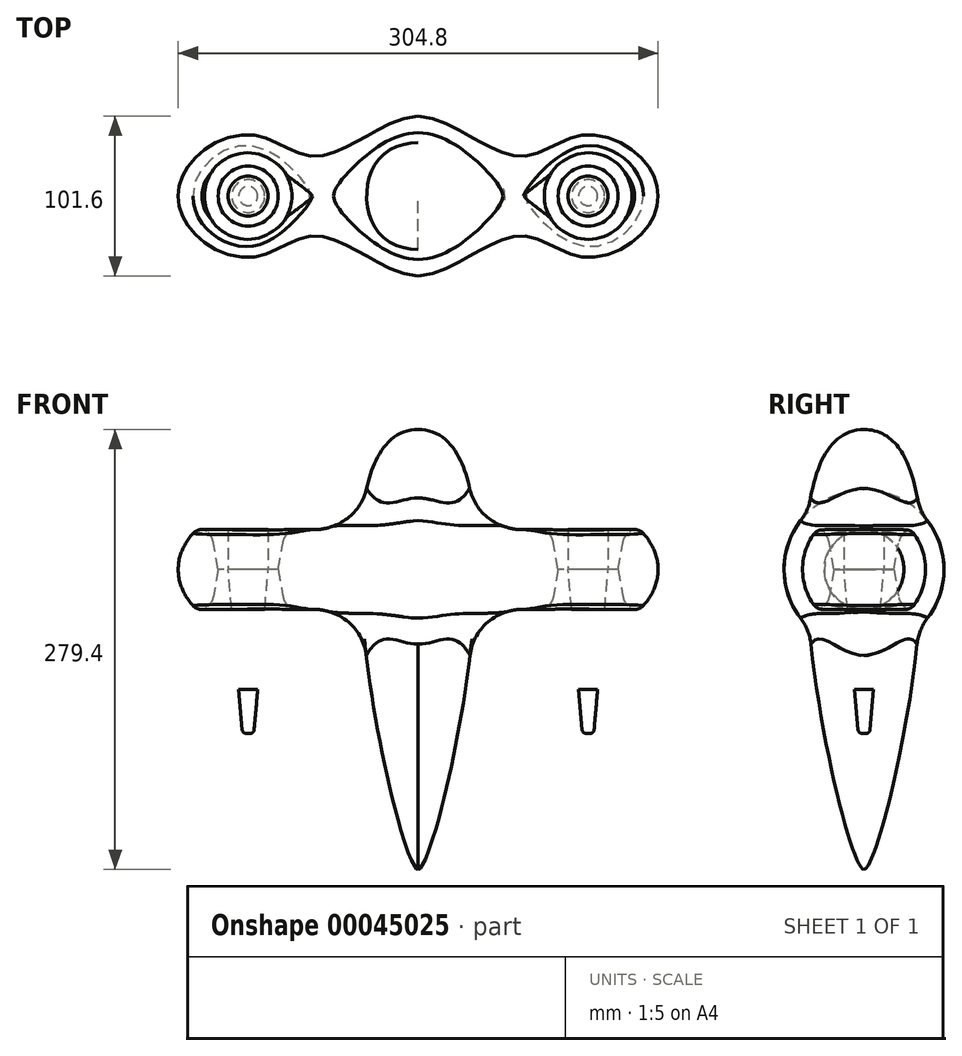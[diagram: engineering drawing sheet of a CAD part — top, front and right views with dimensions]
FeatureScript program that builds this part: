
annotation { "Feature Type Name" : "Feature", "Feature Type Description" : "" }
export const myFeature = defineFeature(function(context is Context, id is Id, definition is map)
    precondition{}
    {
        {
            var Q0;
            Q0=qCreatedBy(makeId("Front.planeOp"),FACE);
            var sketch = newSketch(context, id + "F0", { "sketchPlane" : qUnion([Q0])});
            skLineSegment(sketch, "E0", {"start": v(0, 0) * mm, "end": v(0, 0) * mm});
            skLineSegment(sketch, "E1", {"start": v(0, 0) * mm, "end": v(0, 50.8) * mm});
            skFitSpline(sketch, "E2", {"points": [v(0, 50.8) * mm, v(63.5, 25.4) * mm, v(107.95, 39) * mm, v(152.4, 0) * mm], "startDerivative": vector(157.4, 0) * mm, "endDerivative": vector(0, -203.14) * mm});
            skLineSegment(sketch, "E3", {"start": v(0, 0) * mm, "end": v(152.4, 0) * mm});
            skSolve(sketch);
        }
        {
            var Q0;
            Q0 = qSketchRegion(id + "F0", true);
            var Q1;
            Q1=sQuery(id+"F0.wireOp",EDGE,"E3");
            revolve(context, id + "F1", {"entities" : qUnion([Q0]), "axis" : qUnion([Q1]), "revolveType" : RevolveType.FULL});
        }
        {
            var Q0;
            Q0=makeQuery(id+"F1.opRevolve","SWEPT_BODY",BODY,{"disambiguationData":[OSD([sQuery(id+"F0.wireOp",EDGE,"E0"),sQuery(id+"F0.wireOp",EDGE,"E1"),sQuery(id+"F0.wireOp",EDGE,"E2"),sQuery(id+"F0.wireOp",EDGE,"E3")])]});
            var Q1;
            Q1=makeQuery(id+"F1.opRevolve","SWEPT_FACE",FACE,{"disambiguationData":[OSD([sQuery(id+"F0.wireOp",EDGE,"E1")])]});
            mirror(context, id + "F2", {"operationType" : NewBodyOperationType.ADD, "entities" : qUnion([Q0]), "mirrorPlane" : qUnion([Q1])});
        }
        {
            var Q0;
            Q0=qCreatedBy(makeId("Top.planeOp"),FACE);
            var sketch = newSketch(context, id + "F3", { "sketchPlane" : qUnion([Q0])});
            skCircle(sketch, "E4", {"center": v(-107.95, 0) * mm, "radius": 19.05 * mm});
            skCircle(sketch, "E5", {"center": v(107.95, 0) * mm, "radius": 19.05 * mm});
            skLineSegment(sketch, "E6", {"start": v(-107.95, 0) * mm, "end": v(107.95, 0) * mm, "construction": true});
            skSolve(sketch);
        }
        {
            var Q0;
            Q0 = qSketchRegion(id + "F3", true);
            extrude(context, id + "F4", {"entities" : qUnion([Q0]), "operationType" : NewBodyOperationType.REMOVE, "endBound" : BoundingType.THROUGH_ALL, "depth" : 76.2 * mm, "hasDraft" : true, "draftAngle" : 10 * degree, "hasSecondDirection" : true, "secondDirectionBound" : SecondDirectionBoundingType.THROUGH_ALL, "secondDirectionOppositeDirection" : true, "secondDirectionDepth" : 25.4 * mm, "hasSecondDirectionDraft" : true, "secondDirectionDraftAngle" : 10 * degree});
        }
        {
            var Q0;
            Q0=qCreatedBy(makeId("Top.planeOp"),FACE);
            var sketch = newSketch(context, id + "F5", { "sketchPlane" : qUnion([Q0])});
            skCircle(sketch, "E7", {"center": v(-107.95, 0) * mm, "radius": 12.7 * mm});
            skCircle(sketch, "E8", {"center": v(107.95, 0) * mm, "radius": 12.7 * mm});
            skSolve(sketch);
        }
        {
            var Q0;
            Q0 = qSketchRegion(id + "F5", true);
            extrude(context, id + "F6", {"entities" : qUnion([Q0]), "depth" : 50.8 * mm, "hasSecondDirection" : true, "secondDirectionOppositeDirection" : true, "secondDirectionDepth" : 104.14 * mm, "hasSecondDirectionDraft" : true, "secondDirectionDraftAngle" : 5 * degree, "secondDirectionDraftPullDirection" : true});
        }
        {
            var Q0;
            Q0=makeQuery(id+"F6.opExtrude","CAP_EDGE",EDGE,{"disambiguationData":[OSD([sQuery(id+"F5.wireOp",EDGE,"E7")])],"isStart":false});
            var Q1;
            Q1=makeQuery(id+"F6.opExtrude","CAP_EDGE",EDGE,{"disambiguationData":[OSD([sQuery(id+"F5.wireOp",EDGE,"E8")])],"isStart":false});
            fillet(context, id + "F7", {"entities" : qUnion([Q0, Q1]), "radius" : 12.7 * mm, "tangentPropagation" : true, "allowEdgeOverflow" : false});
        }
        {
            var Q0;
            Q0=makeQuery(id+"F6.opExtrude","CAP_EDGE",EDGE,{"disambiguationData":[OSD([sQuery(id+"F5.wireOp",EDGE,"E7")])],"isStart":true});
            var Q1;
            Q1=makeQuery(id+"F6.opExtrude","CAP_EDGE",EDGE,{"disambiguationData":[OSD([sQuery(id+"F5.wireOp",EDGE,"E8")])],"isStart":true});
            fillet(context, id + "F8", {"entities" : qUnion([Q0, Q1]), "radius" : 2.54 * mm, "tangentPropagation" : true, "allowEdgeOverflow" : false});
        }
        {
            var Q0;
            Q0=qCreatedBy(makeId("Right.planeOp"),FACE);
            var sketch = newSketch(context, id + "F9", { "sketchPlane" : qUnion([Q0])});
            skLineSegment(sketch, "E9", {"start": v(0, 88.9) * mm, "end": v(0, -190.5) * mm});
            skFitSpline(sketch, "E10", {"points": [v(0, 88.9) * mm, v(0, -190.5) * mm], "startDerivative": vector(-228.6, 0) * mm, "endDerivative": vector(38.1, 0) * mm});
            skSolve(sketch);
        }
        {
            var Q0;
            Q0 = qSketchRegion(id + "F9", true);
            var Q1;
            Q1=sQuery(id+"F9.wireOp",EDGE,"E9");
            revolve(context, id + "F10", {"entities" : qUnion([Q0]), "axis" : qUnion([Q1]), "revolveType" : RevolveType.FULL});
        }
        {
            var Q0;
            Q0=makeQuery(id+"F10.opRevolve","SWEPT_BODY",BODY,{"disambiguationData":[OSD([sQuery(id+"F9.wireOp",EDGE,"E9"),sQuery(id+"F9.wireOp",EDGE,"E10")])]});
            var Q1;
            Q1=makeQuery(id+"F1.opRevolve","SWEPT_BODY",BODY,{"disambiguationData":[OSD([sQuery(id+"F0.wireOp",EDGE,"E1"),sQuery(id+"F0.wireOp",EDGE,"E2"),sQuery(id+"F0.wireOp",EDGE,"E3")])]});
            booleanBodies(context, id + "F11", {"operationType" : BooleanOperationType.UNION, "tools" : qUnion([Q0, Q1])});
        }
        {
            var Q0;
            Q0=makeQuery(id+"F11.opBoolean","INTERSECT",EDGE,{"disambiguationData":[OD(1.0)],"derivedFrom":[makeQuery(id+"F2.opPattern","COPY",FACE,{"derivedFrom":makeQuery(id+"F1.opRevolve","SWEPT_FACE",FACE,{"disambiguationData":[OSD([sQuery(id+"F0.wireOp",EDGE,"E2")])]}),"instanceName":"1"}),makeQuery(id+"F10.opRevolve","SWEPT_FACE",FACE,{"disambiguationData":[OSD([sQuery(id+"F9.wireOp",EDGE,"E10")])]})]});
            var Q1;
            Q1=makeQuery(id+"F11.opBoolean","INTERSECT",EDGE,{"disambiguationData":[OD(0.0)],"derivedFrom":[makeQuery(id+"F2.opPattern","COPY",FACE,{"derivedFrom":makeQuery(id+"F1.opRevolve","SWEPT_FACE",FACE,{"disambiguationData":[OSD([sQuery(id+"F0.wireOp",EDGE,"E2")])]}),"instanceName":"1"}),makeQuery(id+"F10.opRevolve","SWEPT_FACE",FACE,{"disambiguationData":[OSD([sQuery(id+"F9.wireOp",EDGE,"E10")])]})]});
            fillet(context, id + "F12", {"entities" : qUnion([Q0, Q1]), "radius" : 33.02 * mm, "tangentPropagation" : true, "allowEdgeOverflow" : false});
        }
        {
            var Q0;
            Q0=qCreatedBy(makeId("Top.planeOp"),FACE);
            cPlane(context, id + "F13", {"entities" : qUnion([Q0]), "cplaneType" : CPlaneType.OFFSET, "offset" : 101.6 * mm, "width" : 152.4 * mm, "height" : 152.4 * mm});
        }
        {
            var Q0;
            Q0=qCreatedBy(id+"F13.planeOp",FACE);
            var sketch = newSketch(context, id + "F14", { "sketchPlane" : qUnion([Q0])});
            skCircle(sketch, "E11", {"center": v(-107.95, 0) * mm, "radius": 44.45 * mm});
            skCircle(sketch, "E12", {"center": v(107.95, 0) * mm, "radius": 44.45 * mm});
            skLineSegment(sketch, "E13", {"start": v(-107.95, 0) * mm, "end": v(107.95, 0) * mm});
            skSolve(sketch);
        }
        {
            var Q0;
            Q0 = qSketchRegion(id + "F14", true);
            extrude(context, id + "F15", {"entities" : qUnion([Q0]), "operationType" : NewBodyOperationType.REMOVE, "oppositeDirection" : true, "depth" : 76.2 * mm});
        }
        {
            var Q0;
            Q0=qCreatedBy(makeId("Top.planeOp"),FACE);
            cPlane(context, id + "F16", {"entities" : qUnion([Q0]), "cplaneType" : CPlaneType.OFFSET, "offset" : 76.2 * mm, "oppositeDirection" : true, "width" : 152.4 * mm, "height" : 152.4 * mm});
        }
        {
            var Q0;
            Q0=qCreatedBy(id+"F16.planeOp",FACE);
            var sketch = newSketch(context, id + "F17", { "sketchPlane" : qUnion([Q0])});
            skCircle(sketch, "E14.0", {"center": v(-107.95, 0) * mm, "radius": 44.45 * mm});
            skCircle(sketch, "E14.1", {"center": v(107.95, 0) * mm, "radius": 44.45 * mm});
            skLineSegment(sketch, "E14.2", {"start": v(-107.95, 0) * mm, "end": v(107.95, 0) * mm, "construction": true});
            skSolve(sketch);
        }
        {
            var Q0;
            Q0 = qSketchRegion(id + "F17", true);
            extrude(context, id + "F18", {"entities" : qUnion([Q0]), "operationType" : NewBodyOperationType.REMOVE, "depth" : 50.8 * mm});
        }
        {
            var Q0;
            Q0=makeQuery(id+"F15.boolean.opBoolean","INTERSECT",EDGE,{"derivedFrom":[makeQuery(id+"F4.boolean.opBoolean","COPY",FACE,{"derivedFrom":makeQuery(id+"F4.split0.splitOp","SPLIT",FACE,{"derivedFrom":makeQuery(id+"F4.opExtrude","SWEPT_FACE",FACE,{"disambiguationData":[OSD([sQuery(id+"F3.wireOp",EDGE,"E4")])]})})}),makeQuery(id+"F15.opExtrude","CAP_FACE",FACE,{"disambiguationData":[OSD([sQuery(id+"F14.wireOp",EDGE,"E11")])],"isStart":false})]});
            var Q1;
            Q1=makeQuery(id+"F15.boolean.opBoolean","INTERSECT",EDGE,{"derivedFrom":[makeQuery(id+"F4.boolean.opBoolean","COPY",FACE,{"derivedFrom":makeQuery(id+"F4.split1.splitOp","SPLIT",FACE,{"derivedFrom":makeQuery(id+"F4.opExtrude","SWEPT_FACE",FACE,{"disambiguationData":[OSD([sQuery(id+"F3.wireOp",EDGE,"E5")])]})})}),makeQuery(id+"F15.opExtrude","CAP_FACE",FACE,{"disambiguationData":[OSD([sQuery(id+"F14.wireOp",EDGE,"E12")])],"isStart":false})]});
            var Q2;
            Q2=makeQuery(id+"F18.boolean.opBoolean","INTERSECT",EDGE,{"derivedFrom":[makeQuery(id+"F4.boolean.opBoolean","COPY",FACE,{"derivedFrom":makeQuery(id+"F4.split0.splitOp","SPLIT",FACE,{"derivedFrom":makeQuery(id+"F4.opExtrude","SWEPT_FACE",FACE,{"disambiguationData":[OSD([sQuery(id+"F3.wireOp",EDGE,"E4")])]}),"isFromBackBody":true})}),makeQuery(id+"F18.opExtrude","CAP_FACE",FACE,{"disambiguationData":[OSD([sQuery(id+"F17.wireOp",EDGE,"E14.0")])],"isStart":false})]});
            var Q3;
            Q3=makeQuery(id+"F18.boolean.opBoolean","INTERSECT",EDGE,{"derivedFrom":[makeQuery(id+"F4.boolean.opBoolean","COPY",FACE,{"derivedFrom":makeQuery(id+"F4.split1.splitOp","SPLIT",FACE,{"derivedFrom":makeQuery(id+"F4.opExtrude","SWEPT_FACE",FACE,{"disambiguationData":[OSD([sQuery(id+"F3.wireOp",EDGE,"E5")])]}),"isFromBackBody":true})}),makeQuery(id+"F18.opExtrude","CAP_FACE",FACE,{"disambiguationData":[OSD([sQuery(id+"F17.wireOp",EDGE,"E14.1")])],"isStart":false})]});
            chamfer(context, id + "F19", {"entities" : qUnion([Q0, Q1, Q2, Q3]), "width" : 5.08 * mm, "tangentPropagation" : true});
        }
        {
            var Q0;
            Q0=makeQuery(id+"F15.boolean.opBoolean","INTERSECT",EDGE,{"derivedFrom":[makeQuery(id+"F2.opPattern","COPY",FACE,{"derivedFrom":makeQuery(id+"F1.opRevolve","SWEPT_FACE",FACE,{"disambiguationData":[OSD([sQuery(id+"F0.wireOp",EDGE,"E2")])]}),"instanceName":"1"}),makeQuery(id+"F15.opExtrude","CAP_FACE",FACE,{"disambiguationData":[OSD([sQuery(id+"F14.wireOp",EDGE,"E11")])],"isStart":false})]});
            var Q1;
            Q1=makeQuery(id+"F15.boolean.opBoolean","INTERSECT",EDGE,{"derivedFrom":[makeQuery(id+"F1.opRevolve","SWEPT_FACE",FACE,{"disambiguationData":[OSD([sQuery(id+"F0.wireOp",EDGE,"E2")])]}),makeQuery(id+"F15.opExtrude","CAP_FACE",FACE,{"disambiguationData":[OSD([sQuery(id+"F14.wireOp",EDGE,"E12")])],"isStart":false})]});
            var Q2;
            Q2=makeQuery(id+"F18.boolean.opBoolean","INTERSECT",EDGE,{"derivedFrom":[makeQuery(id+"F1.opRevolve","SWEPT_FACE",FACE,{"disambiguationData":[OSD([sQuery(id+"F0.wireOp",EDGE,"E2")])]}),makeQuery(id+"F18.opExtrude","CAP_FACE",FACE,{"disambiguationData":[OSD([sQuery(id+"F17.wireOp",EDGE,"E14.1")])],"isStart":false})]});
            var Q3;
            Q3=makeQuery(id+"F18.boolean.opBoolean","INTERSECT",EDGE,{"derivedFrom":[makeQuery(id+"F2.opPattern","COPY",FACE,{"derivedFrom":makeQuery(id+"F1.opRevolve","SWEPT_FACE",FACE,{"disambiguationData":[OSD([sQuery(id+"F0.wireOp",EDGE,"E2")])]}),"instanceName":"1"}),makeQuery(id+"F18.opExtrude","CAP_FACE",FACE,{"disambiguationData":[OSD([sQuery(id+"F17.wireOp",EDGE,"E14.0")])],"isStart":false})]});
            fillet(context, id + "F20", {"entities" : qUnion([Q0, Q1, Q2, Q3]), "radius" : 7.62 * mm, "tangentPropagation" : true, "allowEdgeOverflow" : false});
        }
        {
            var Q0;
            {var subQ0=makeQuery(id+"F4.boolean.opBoolean","COPY",FACE,{"derivedFrom":makeQuery(id+"F4.split0.splitOp","SPLIT",FACE,{"derivedFrom":makeQuery(id+"F4.opExtrude","SWEPT_FACE",FACE,{"disambiguationData":[OSD([sQuery(id+"F3.wireOp",EDGE,"E4")])]})})});Q0=makeQuery(id+"F19.opChamfer","BLEND_EDGE",EDGE,{"blendedFrom":[makeQuery(id+"F15.boolean.opBoolean","INTERSECT",EDGE,{"derivedFrom":[subQ0,makeQuery(id+"F15.opExtrude","CAP_FACE",FACE,{"disambiguationData":[OSD([sQuery(id+"F14.wireOp",EDGE,"E11")])],"isStart":false})]}),subQ0],"blendedInto":[subQ0]});}
            var Q1;
            {var subQ0=makeQuery(id+"F4.boolean.opBoolean","COPY",FACE,{"derivedFrom":makeQuery(id+"F4.split1.splitOp","SPLIT",FACE,{"derivedFrom":makeQuery(id+"F4.opExtrude","SWEPT_FACE",FACE,{"disambiguationData":[OSD([sQuery(id+"F3.wireOp",EDGE,"E5")])]})})});Q1=makeQuery(id+"F19.opChamfer","BLEND_EDGE",EDGE,{"blendedFrom":[makeQuery(id+"F15.boolean.opBoolean","INTERSECT",EDGE,{"derivedFrom":[subQ0,makeQuery(id+"F15.opExtrude","CAP_FACE",FACE,{"disambiguationData":[OSD([sQuery(id+"F14.wireOp",EDGE,"E12")])],"isStart":false})]}),subQ0],"blendedInto":[subQ0]});}
            var Q2;
            {var subQ0=makeQuery(id+"F4.opExtrude","SWEPT_FACE",FACE,{"disambiguationData":[OSD([sQuery(id+"F3.wireOp",EDGE,"E5")])]});Q2=makeQuery(id+"F4.boolean.opBoolean","COPY",EDGE,{"derivedFrom":makeQuery(id+"F4.booleanUnion1.opBoolean","MERGE",EDGE,{"derivedFrom":[makeQuery(id+"F4.split1.splitOp","SPLIT_SURFACE_INTERSECT",EDGE,{"derivedFrom":[subQ0]}),makeQuery(id+"F4.split1.splitOp","SPLIT_SURFACE_INTERSECT",EDGE,{"derivedFrom":[subQ0],"isFromBackBody":true})]})});}
            var Q3;
            {var subQ0=makeQuery(id+"F4.opExtrude","SWEPT_FACE",FACE,{"disambiguationData":[OSD([sQuery(id+"F3.wireOp",EDGE,"E4")])]});Q3=makeQuery(id+"F4.boolean.opBoolean","COPY",EDGE,{"derivedFrom":makeQuery(id+"F4.booleanUnion0.opBoolean","MERGE",EDGE,{"derivedFrom":[makeQuery(id+"F4.split0.splitOp","SPLIT_SURFACE_INTERSECT",EDGE,{"derivedFrom":[subQ0]}),makeQuery(id+"F4.split0.splitOp","SPLIT_SURFACE_INTERSECT",EDGE,{"derivedFrom":[subQ0],"isFromBackBody":true})]})});}
            var Q4;
            {var subQ0=makeQuery(id+"F4.boolean.opBoolean","COPY",FACE,{"derivedFrom":makeQuery(id+"F4.split0.splitOp","SPLIT",FACE,{"derivedFrom":makeQuery(id+"F4.opExtrude","SWEPT_FACE",FACE,{"disambiguationData":[OSD([sQuery(id+"F3.wireOp",EDGE,"E4")])]}),"isFromBackBody":true})});Q4=makeQuery(id+"F19.opChamfer","BLEND_EDGE",EDGE,{"blendedFrom":[makeQuery(id+"F18.boolean.opBoolean","INTERSECT",EDGE,{"derivedFrom":[subQ0,makeQuery(id+"F18.opExtrude","CAP_FACE",FACE,{"disambiguationData":[OSD([sQuery(id+"F17.wireOp",EDGE,"E14.0")])],"isStart":false})]}),subQ0],"blendedInto":[subQ0]});}
            var Q5;
            {var subQ0=makeQuery(id+"F4.boolean.opBoolean","COPY",FACE,{"derivedFrom":makeQuery(id+"F4.split1.splitOp","SPLIT",FACE,{"derivedFrom":makeQuery(id+"F4.opExtrude","SWEPT_FACE",FACE,{"disambiguationData":[OSD([sQuery(id+"F3.wireOp",EDGE,"E5")])]}),"isFromBackBody":true})});Q5=makeQuery(id+"F19.opChamfer","BLEND_EDGE",EDGE,{"blendedFrom":[makeQuery(id+"F18.boolean.opBoolean","INTERSECT",EDGE,{"derivedFrom":[subQ0,makeQuery(id+"F18.opExtrude","CAP_FACE",FACE,{"disambiguationData":[OSD([sQuery(id+"F17.wireOp",EDGE,"E14.1")])],"isStart":false})]}),subQ0],"blendedInto":[subQ0]});}
            fillet(context, id + "F21", {"entities" : qUnion([Q0, Q1, Q2, Q3, Q4, Q5]), "radius" : 12.7 * mm, "tangentPropagation" : true, "allowEdgeOverflow" : false});
        }
    });
